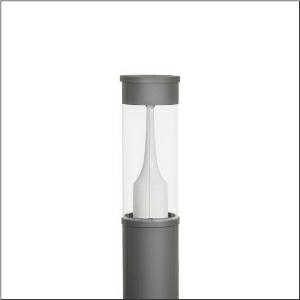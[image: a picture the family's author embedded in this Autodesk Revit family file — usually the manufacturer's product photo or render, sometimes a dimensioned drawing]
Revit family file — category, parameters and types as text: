
# Revit family: city-light_120_iq___pl1_2s_5xa5285of14h_ee05
name_source: partatom
category: Lighting Fixtures
units: mm (PartAtom-declared; Revit-internal decimal feet)

## family parameters
Cut with Voids When Loaded = No
Host = Face
Light Source = No
Part Type = Normal
Room Calculation Point = No
Round Connector Dimension = Use Diameter
Shared = No

## types (1)
- --- (1 x LED, 2970 lm, 21.8 W, 2700K)
    Apparent Load = 22 VA
    CIE Flux Codes = 23 62 94 96 100
    Color Rendering = 70
    Color Temperature = 2700K
    Default Elevation = 1800 mm
    Description = City-Light 120 iQ, bollard luminaire, Module 540 iQ-SR, primary light control with 3 zone facetted reflector, of plastic, silver coated, highly specular, structured, primary optical cover: cover, of PMMA, transparent, partly coated, light distribution: PL1.2s, primary light characteristic: symmetric, LED, High Power LED, rated luminous flux: 2.970lm, luminous efficacy: 136lm/W, light colour: 727, colour temperature: 2700K, control gear: iQ Street-Remote, control: pre-setting: logarithmic dimming characteristic, Street-Remote, Auto-Match, Temp-Guard, Lumen-Switch, Night-Set, Smart-Wire, Light-Fading, Desk-Remote (wireless, voltage-free reading and setting of iQ features in the workshop via application-optimized NFC function/RFID function), optimised constant luminous flux control (CLO 2.0), with terminal, 6-pole, max. 2.5mm², mains connection: 230..240V, AC, 50/60Hz, start of lifetime: 22W, end of service life: 23W, reduction: 11W, luminaire housing, cylindrical, of extruded aluminium section, coated, Siteco® metallic grey (DB 702S), length: 1.200mm, diameter: 200mm, Module 540 iQ-SR, traffic white (RAL 9016), equipment: standard, protection rating (complete): IP54, insulation class (complete): insulation class II (safety insulation), certification: CE, ENEC, VDE, packaging unit: 1 piece

Light Distribution: PL1.2s
    Height = 500 mm
    Lamp = 1 x LED
    Lamp Light Flux = 2970 lm
    Lamp Power = 21.8 W
    Lamp count = 1
    Length = 200 mm  [stored 0.656168 ft]
    Luminous efficacy = 136 lm/W
    Manufacturer = Siteco
    ModVariant = No
    Model = 5XA5285OF14H
    Mounting Place = Floor
    Mounting Type = Freestanding
    Number of Poles = 1
    OnlyDefault = Yes
    Power Factor = 1
    Product Name = City-Light 120 iQ | PL1.2s
    Product group = bollard luminaire
    ProductGroupID = 1304
    Protection Class = Protection class II
    Protection Degree = IP 54
    RLX_Detail_Level = 1
    RLX_Emergency_Light_Flux = 0 lm
    RLX_Emergency_Type = 0
    RLX_Emergency_Type_DB = No
    RlxData = <blob elided: 22337 chars, md5=395d35f9>
    Socket = socket
    Standby Power = 0 W
    System Light Flux = 2970 lm
    System Power = 22 W
    Type Comments = factory setting: luminous flux: 100 % | dim-lin: 254 | 456 mA
    Type Image = l_1006922.jpg
    URL = http://relux.com
    VarID = @adj_166601
    Voltage = 0 V
    Weight = 0.00 kg
    Width = 0 mm  [stored 0 ft]

note: [stored X ft] marks values corroborated as IEEE doubles in the binary element streams (Revit-internal decimal feet)

## geometry (parser evidence)
native form markers: Blend x4, Sweep x11
no freeform markers — native parametric forms only
